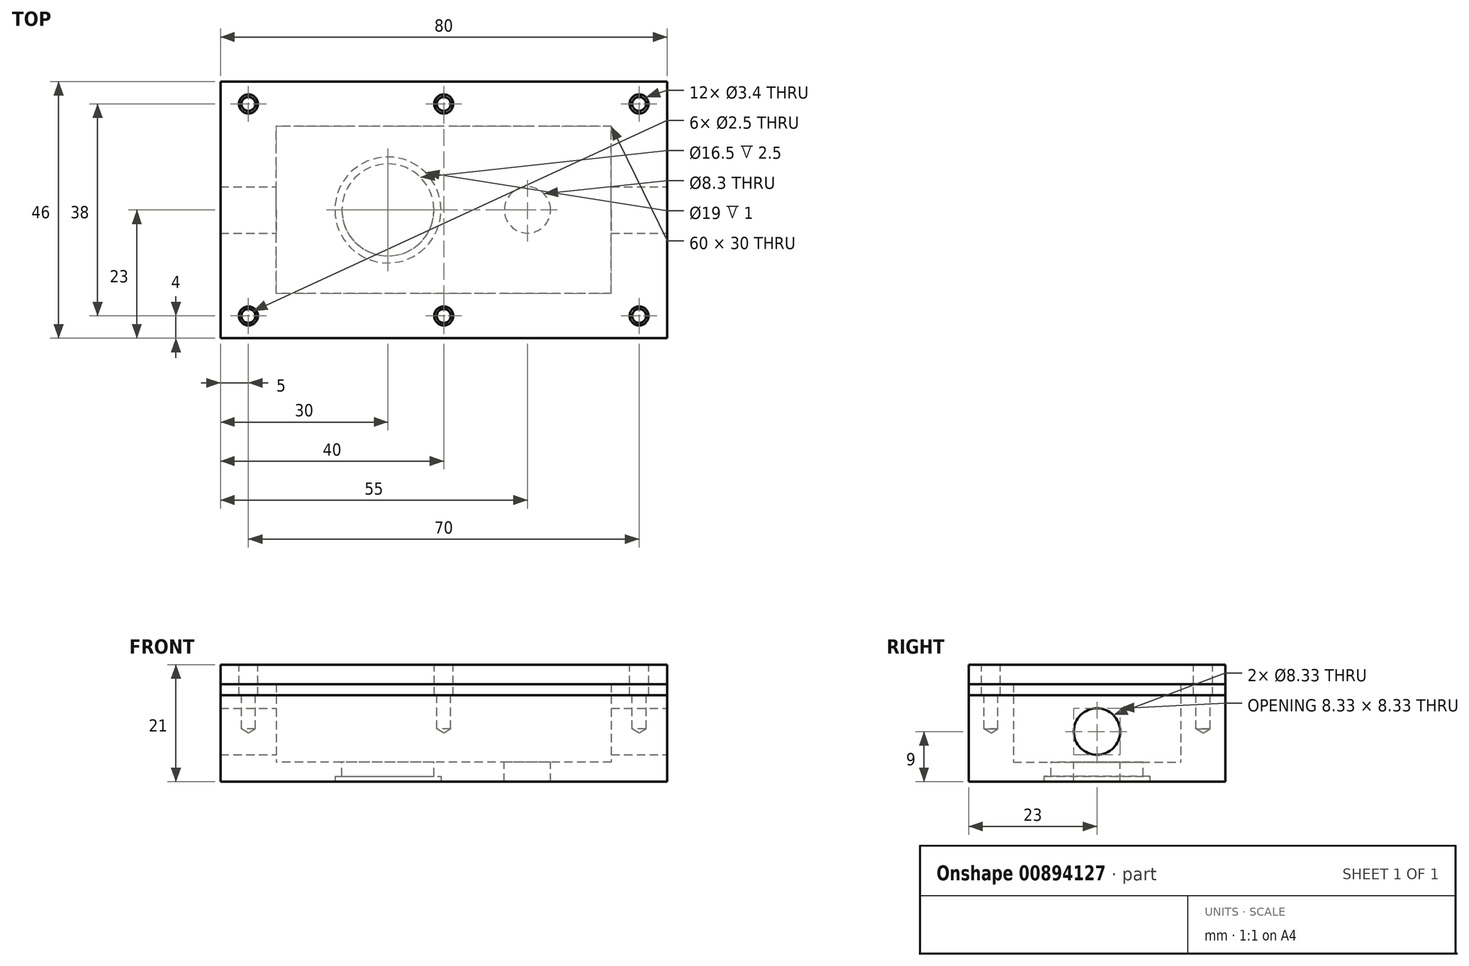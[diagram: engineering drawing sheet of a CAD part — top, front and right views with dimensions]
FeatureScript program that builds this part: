
annotation { "Feature Type Name" : "Feature", "Feature Type Description" : "" }
export const myFeature = defineFeature(function(context is Context, id is Id, definition is map)
    precondition{}
    {
        {
            var Q0;
            Q0=qCreatedBy(makeId("Top.planeOp"),FACE);
            var sketch = newSketch(context, id + "F0", { "sketchPlane" : qUnion([Q0])});
            skCircle(sketch, "E0", {"center": v(0, 0) * mm, "radius": 9.5 * mm});
            skCircle(sketch, "E1", {"center": v(0, 0) * mm, "radius": 8.25 * mm});
            skCircle(sketch, "E2", {"center": v(25, 0) * mm, "radius": 4.62 * mm});
            skCircle(sketch, "E3", {"center": v(25, 0) * mm, "radius": 4.15 * mm});
            skLineSegment(sketch, "E4.bottom", {"start": v(40, -15) * mm, "end": v(-20, -15) * mm});
            skLineSegment(sketch, "E4.top", {"start": v(40, 15) * mm, "end": v(-20, 15) * mm});
            skLineSegment(sketch, "E4.left", {"start": v(40, -15) * mm, "end": v(40, 15) * mm});
            skLineSegment(sketch, "E4.right", {"start": v(-20, -15) * mm, "end": v(-20, 15) * mm});
            skLineSegment(sketch, "E5.bottom", {"start": v(50, -23) * mm, "end": v(-30, -23) * mm});
            skLineSegment(sketch, "E5.top", {"start": v(50, 23) * mm, "end": v(-30, 23) * mm});
            skLineSegment(sketch, "E5.left", {"start": v(50, -23) * mm, "end": v(50, 23) * mm});
            skLineSegment(sketch, "E5.right", {"start": v(-30, -23) * mm, "end": v(-30, 23) * mm});
            skSolve(sketch);
        }
        {
            var Q0;
            Q0=qCreatedBy(makeId("Top.planeOp"),FACE);
            var sketch = newSketch(context, id + "F1", { "sketchPlane" : qUnion([Q0])});
            skLineSegment(sketch, "E6.0", {"start": v(50, 23) * mm, "end": v(-30, 23) * mm});
            skLineSegment(sketch, "E7.0", {"start": v(-30, -23) * mm, "end": v(-30, 23) * mm});
            skLineSegment(sketch, "E8.0", {"start": v(50, -23) * mm, "end": v(-30, -23) * mm});
            skLineSegment(sketch, "E9.0", {"start": v(50, -23) * mm, "end": v(50, 23) * mm});
            skLineSegment(sketch, "E10", {"start": v(10, 23) * mm, "end": v(10, -23) * mm, "construction": true});
            skLineSegment(sketch, "E11", {"start": v(-30, 0) * mm, "end": v(50, 0) * mm, "construction": true});
            skLineSegment(sketch, "E12", {"start": v(-25, 23) * mm, "end": v(-25, -23) * mm, "construction": true});
            skLineSegment(sketch, "E13", {"start": v(45, -23) * mm, "end": v(45, 23) * mm, "construction": true});
            skCircle(sketch, "E14", {"center": v(10, 19) * mm, "radius": 1.25 * mm});
            skCircle(sketch, "E15", {"center": v(45, 19) * mm, "radius": 1.25 * mm});
            skCircle(sketch, "E16", {"center": v(-25, 19) * mm, "radius": 1.25 * mm});
            skCircle(sketch, "E17.MirrorC", {"center": v(-25, -19) * mm, "radius": 1.25 * mm});
            skCircle(sketch, "E18.MirrorC", {"center": v(10, -19) * mm, "radius": 1.25 * mm});
            skCircle(sketch, "E19.MirrorC", {"center": v(45, -19) * mm, "radius": 1.25 * mm});
            skSolve(sketch);
        }
        {
            var Q0;
            Q0=qCreatedBy(makeId("Top.planeOp"),FACE);
            cPlane(context, id + "F2", {"entities" : qUnion([Q0]), "cplaneType" : CPlaneType.OFFSET, "offset" : 12 * mm, "width" : 150 * mm, "height" : 150 * mm});
        }
        {
            var Q0;
            Q0=qCreatedBy(makeId("Top.planeOp"),FACE);
            var sketch = newSketch(context, id + "F3", { "sketchPlane" : qUnion([Q0])});
            skLineSegment(sketch, "E20.0", {"start": v(50, -23) * mm, "end": v(-30, -23) * mm});
            skLineSegment(sketch, "E21.0", {"start": v(50, -23) * mm, "end": v(50, 23) * mm});
            skLineSegment(sketch, "E22.0", {"start": v(50, 23) * mm, "end": v(-30, 23) * mm});
            skLineSegment(sketch, "E23.0", {"start": v(-30, -23) * mm, "end": v(-30, 23) * mm});
            skSolve(sketch);
        }
        {
            var Q0;
            Q0 = qSketchRegion(id + "F3", true);
            extrude(context, id + "F4", {"entities" : qUnion([Q0]), "oppositeDirection" : true, "depth" : 3.5 * mm, "offsetDistance" : 25 * mm});
        }
        {
            var Q0;
            Q0=qCreatedBy(makeId("Top.planeOp"),FACE);
            var sketch = newSketch(context, id + "F5", { "sketchPlane" : qUnion([Q0])});
            skLineSegment(sketch, "E24.0", {"start": v(50, 23) * mm, "end": v(-30, 23) * mm});
            skLineSegment(sketch, "E25.0", {"start": v(-30, -23) * mm, "end": v(-30, 23) * mm});
            skLineSegment(sketch, "E26.0", {"start": v(-20, -15) * mm, "end": v(-20, 15) * mm});
            skLineSegment(sketch, "E27.0", {"start": v(40, 15) * mm, "end": v(-20, 15) * mm});
            skLineSegment(sketch, "E28.0", {"start": v(40, -15) * mm, "end": v(40, 15) * mm});
            skLineSegment(sketch, "E29.0", {"start": v(40, -15) * mm, "end": v(-20, -15) * mm});
            skLineSegment(sketch, "E30.0", {"start": v(50, -23) * mm, "end": v(-30, -23) * mm});
            skLineSegment(sketch, "E31.0", {"start": v(50, -23) * mm, "end": v(50, 23) * mm});
            skSolve(sketch);
        }
        {
            var Q0;
            Q0 = qSketchRegion(id + "F5", true);
            var Q1;
            Q1=qCreatedBy(id+"F2.planeOp",FACE);
            extrude(context, id + "F6", {"entities" : qUnion([Q0]), "operationType" : NewBodyOperationType.ADD, "endBound" : BoundingType.UP_TO_SURFACE, "depth" : 25 * mm, "endBoundEntityFace" : qUnion([Q1]), "offsetDistance" : 25 * mm});
        }
        {
            var Q0;
            Q0=qCreatedBy(makeId("Top.planeOp"),FACE);
            var sketch = newSketch(context, id + "F7", { "sketchPlane" : qUnion([Q0])});
            skCircle(sketch, "E32.0", {"center": v(25, 0) * mm, "radius": 4.15 * mm});
            skCircle(sketch, "E33.0", {"center": v(0, 0) * mm, "radius": 8.25 * mm});
            skSolve(sketch);
        }
        {
            var Q0;
            Q0 = qSketchRegion(id + "F7", true);
            extrude(context, id + "F8", {"entities" : qUnion([Q0]), "operationType" : NewBodyOperationType.REMOVE, "oppositeDirection" : true, "depth" : 25 * mm, "offsetDistance" : 25 * mm});
        }
        {
            var Q0;
            Q0=makeQuery(id+"F4.opExtrude","CAP_FACE",FACE,{"disambiguationData":[OSD([sQuery(id+"F3.wireOp",EDGE,"E20.0"),sQuery(id+"F3.wireOp",EDGE,"E21.0"),sQuery(id+"F3.wireOp",EDGE,"E22.0"),sQuery(id+"F3.wireOp",EDGE,"E23.0")])],"isStart":false});
            var sketch = newSketch(context, id + "F9", { "sketchPlane" : qUnion([Q0])});
            skCircle(sketch, "E34.0", {"center": v(0, 0) * mm, "radius": 9.5 * mm});
            skSolve(sketch);
        }
        {
            var Q0;
            Q0 = qSketchRegion(id + "F9", true);
            extrude(context, id + "F10", {"entities" : qUnion([Q0]), "operationType" : NewBodyOperationType.REMOVE, "oppositeDirection" : true, "depth" : 1 * mm, "offsetDistance" : 25 * mm});
        }
        {
            var Q0;
            Q0=makeQuery(id+"F6.boolean.opBoolean","MERGE",FACE,{"derivedFrom":[makeQuery(id+"F4.opExtrude","SWEPT_FACE",FACE,{"disambiguationData":[OSD([sQuery(id+"F3.wireOp",EDGE,"E21.0")])]}),makeQuery(id+"F6.opExtrude","SWEPT_FACE",FACE,{"disambiguationData":[OSD([sQuery(id+"F5.wireOp",EDGE,"E31.0")])]})]});
            cPlane(context, id + "F11", {"entities" : qUnion([Q0]), "cplaneType" : CPlaneType.OFFSET, "offset" : 0 * mm, "width" : 150 * mm, "height" : 150 * mm});
        }
        {
            var Q0;
            Q0=qCreatedBy(id+"F11.planeOp",FACE);
            var sketch = newSketch(context, id + "F12", { "sketchPlane" : qUnion([Q0])});
            skCircle(sketch, "E35", {"center": v(0, 5.5) * mm, "radius": 4.17 * mm});
            skSolve(sketch);
        }
        {
            var Q0;
            Q0=sQuery(id+"F12.wireOp",VERTEX,"E35.center");
            var Q1;
            Q1=makeQuery(id+"F4.opExtrude","SWEPT_BODY",BODY,{"disambiguationData":[OSD([sQuery(id+"F3.wireOp",EDGE,"E20.0"),sQuery(id+"F3.wireOp",EDGE,"E21.0"),sQuery(id+"F3.wireOp",EDGE,"E22.0"),sQuery(id+"F3.wireOp",EDGE,"E23.0")])]});
            hole(context, id + "F13", {"style" : HoleStyle.SIMPLE, "endStyle" : HoleEndStyle.THROUGH, "standardTappedOrClearance" : lookupTablePath({ "fit" : "Standard", "standard" : "ISO", "size" : "M3", "type" : "Clearance" }), "standardBlindInLast" : lookupTablePath({ "fit" : "Standard", "standard" : "ISO", "size" : "M3", "type" : "Clearance" }), "holeDiameter" : 8.33 * mm, "majorDiameter" : 5 * mm, "tappedDepth" : 4.5 * mm, "tapClearance" : 3, "locations" : qUnion([Q0]), "scope" : qUnion([Q1])});
        }
        {
            var Q0;
            Q0=makeQuery(id+"F6.opExtrude","CAP_FACE",FACE,{"disambiguationData":[OSD([sQuery(id+"F5.wireOp",EDGE,"E24.0"),sQuery(id+"F5.wireOp",EDGE,"E25.0"),sQuery(id+"F5.wireOp",EDGE,"E26.0"),sQuery(id+"F5.wireOp",EDGE,"E27.0"),sQuery(id+"F5.wireOp",EDGE,"E28.0"),sQuery(id+"F5.wireOp",EDGE,"E29.0"),sQuery(id+"F5.wireOp",EDGE,"E30.0"),sQuery(id+"F5.wireOp",EDGE,"E31.0")])],"isStart":false});
            var sketch = newSketch(context, id + "F14", { "sketchPlane" : qUnion([Q0])});
            skPoint(sketch, "E36.0", {"position": v(-25, 19) * mm});
            skPoint(sketch, "E37.0", {"position": v(10, 19) * mm});
            skPoint(sketch, "E38.0", {"position": v(45, 19) * mm});
            skPoint(sketch, "E39.0", {"position": v(45, -19) * mm});
            skPoint(sketch, "E40.0", {"position": v(10, -19) * mm});
            skPoint(sketch, "E41.0", {"position": v(-25, -19) * mm});
            skSolve(sketch);
        }
        {
            var Q0;
            Q0=sQuery(id+"F14.wireOp",VERTEX,"E36.0");
            var Q1;
            Q1=sQuery(id+"F14.wireOp",VERTEX,"E41.0");
            var Q2;
            Q2=sQuery(id+"F14.wireOp",VERTEX,"E40.0");
            var Q3;
            Q3=sQuery(id+"F14.wireOp",VERTEX,"E39.0");
            var Q4;
            Q4=sQuery(id+"F14.wireOp",VERTEX,"E38.0");
            var Q5;
            Q5=sQuery(id+"F14.wireOp",VERTEX,"E37.0");
            var Q6;
            Q6=makeQuery(id+"F4.opExtrude","SWEPT_BODY",BODY,{"disambiguationData":[OSD([sQuery(id+"F3.wireOp",EDGE,"E20.0"),sQuery(id+"F3.wireOp",EDGE,"E21.0"),sQuery(id+"F3.wireOp",EDGE,"E22.0"),sQuery(id+"F3.wireOp",EDGE,"E23.0")])]});
            hole(context, id + "F15", {"style" : HoleStyle.SIMPLE, "endStyle" : HoleEndStyle.BLIND, "standardTappedOrClearance" : lookupTablePath({ "standard" : "ISO", "engagement" : "75%", "pitch" : "0.5 mm", "size" : "M3", "type" : "Tapped" }), "standardBlindInLast" : lookupTablePath({ "standard" : "ISO", "engagement" : "75%", "pitch" : "0.5 mm", "size" : "M3", "type" : "Tapped" }), "holeDiameter" : 2.5 * mm, "majorDiameter" : 3 * mm, "showTappedDepth" : true, "holeDepth" : 6 * mm, "tappedDepth" : 4.5 * mm, "tapClearance" : 3, "locations" : qUnion([Q0, Q1, Q2, Q3, Q4, Q5]), "scope" : qUnion([Q6])});
        }
        {
            var Q0;
            Q0=qCreatedBy(id+"F2.planeOp",FACE);
            var sketch = newSketch(context, id + "F16", { "sketchPlane" : qUnion([Q0])});
            skLineSegment(sketch, "E42.0", {"start": v(50, 23) * mm, "end": v(-30, 23) * mm});
            skLineSegment(sketch, "E43.0", {"start": v(-30, -23) * mm, "end": v(-30, 23) * mm});
            skLineSegment(sketch, "E44.0", {"start": v(50, -23) * mm, "end": v(-30, -23) * mm});
            skLineSegment(sketch, "E45.0", {"start": v(50, -23) * mm, "end": v(50, 23) * mm});
            skLineSegment(sketch, "E46.0", {"start": v(40, -15) * mm, "end": v(40, 15) * mm});
            skLineSegment(sketch, "E47.0", {"start": v(40, 15) * mm, "end": v(-20, 15) * mm});
            skLineSegment(sketch, "E48.0", {"start": v(-20, -15) * mm, "end": v(-20, 15) * mm});
            skLineSegment(sketch, "E49.0", {"start": v(40, -15) * mm, "end": v(-20, -15) * mm});
            skSolve(sketch);
        }
        {
            var Q0;
            Q0 = qSketchRegion(id + "F16", true);
            extrude(context, id + "F17", {"entities" : qUnion([Q0]), "depth" : 2 * mm, "offsetDistance" : 25 * mm});
        }
        {
            var Q0;
            Q0=makeQuery(id+"F17.opExtrude","CAP_FACE",FACE,{"disambiguationData":[OSD([sQuery(id+"F16.wireOp",EDGE,"E42.0"),sQuery(id+"F16.wireOp",EDGE,"E43.0"),sQuery(id+"F16.wireOp",EDGE,"E44.0"),sQuery(id+"F16.wireOp",EDGE,"E45.0"),sQuery(id+"F16.wireOp",EDGE,"E46.0"),sQuery(id+"F16.wireOp",EDGE,"E47.0"),sQuery(id+"F16.wireOp",EDGE,"E48.0"),sQuery(id+"F16.wireOp",EDGE,"E49.0")])],"isStart":false});
            var sketch = newSketch(context, id + "F18", { "sketchPlane" : qUnion([Q0])});
            skPoint(sketch, "E50.0", {"position": v(-25, 19) * mm});
            skPoint(sketch, "E51.0", {"position": v(10, 19) * mm});
            skPoint(sketch, "E52.0", {"position": v(45, 19) * mm});
            skPoint(sketch, "E53.0", {"position": v(45, -19) * mm});
            skPoint(sketch, "E54.0", {"position": v(10, -19) * mm});
            skPoint(sketch, "E55.0", {"position": v(-25, -19) * mm});
            skSolve(sketch);
        }
        {
            var Q0;
            Q0=sQuery(id+"F18.wireOp",VERTEX,"E55.0");
            var Q1;
            Q1=sQuery(id+"F18.wireOp",VERTEX,"E54.0");
            var Q2;
            Q2=sQuery(id+"F18.wireOp",VERTEX,"E53.0");
            var Q3;
            Q3=sQuery(id+"F18.wireOp",VERTEX,"E52.0");
            var Q4;
            Q4=sQuery(id+"F18.wireOp",VERTEX,"E51.0");
            var Q5;
            Q5=sQuery(id+"F18.wireOp",VERTEX,"E50.0");
            var Q6;
            Q6=makeQuery(id+"F17.opExtrude","SWEPT_BODY",BODY,{"disambiguationData":[OSD([sQuery(id+"F16.wireOp",EDGE,"E42.0"),sQuery(id+"F16.wireOp",EDGE,"E43.0"),sQuery(id+"F16.wireOp",EDGE,"E44.0"),sQuery(id+"F16.wireOp",EDGE,"E45.0"),sQuery(id+"F16.wireOp",EDGE,"E46.0"),sQuery(id+"F16.wireOp",EDGE,"E47.0"),sQuery(id+"F16.wireOp",EDGE,"E48.0"),sQuery(id+"F16.wireOp",EDGE,"E49.0")])]});
            hole(context, id + "F19", {"style" : HoleStyle.SIMPLE, "endStyle" : HoleEndStyle.THROUGH, "standardTappedOrClearance" : lookupTablePath({ "fit" : "Normal", "standard" : "ISO", "size" : "M3", "type" : "Clearance" }), "standardBlindInLast" : lookupTablePath({ "fit" : "Normal", "standard" : "ISO", "size" : "M3", "type" : "Clearance" }), "holeDiameter" : 3.4 * mm, "majorDiameter" : 3 * mm, "tappedDepth" : 4.5 * mm, "tapClearance" : 3, "locations" : qUnion([Q0, Q1, Q2, Q3, Q4, Q5]), "scope" : qUnion([Q6])});
        }
        {
            var Q0;
            Q0=makeQuery(id+"F17.opExtrude","CAP_FACE",FACE,{"disambiguationData":[OSD([sQuery(id+"F16.wireOp",EDGE,"E42.0"),sQuery(id+"F16.wireOp",EDGE,"E43.0"),sQuery(id+"F16.wireOp",EDGE,"E44.0"),sQuery(id+"F16.wireOp",EDGE,"E45.0"),sQuery(id+"F16.wireOp",EDGE,"E46.0"),sQuery(id+"F16.wireOp",EDGE,"E47.0"),sQuery(id+"F16.wireOp",EDGE,"E48.0"),sQuery(id+"F16.wireOp",EDGE,"E49.0")])],"isStart":false});
            var sketch = newSketch(context, id + "F20", { "sketchPlane" : qUnion([Q0])});
            skLineSegment(sketch, "E56.0", {"start": v(50, -23) * mm, "end": v(-30, -23) * mm});
            skLineSegment(sketch, "E57.0", {"start": v(50, -23) * mm, "end": v(50, 23) * mm});
            skLineSegment(sketch, "E58.0", {"start": v(50, 23) * mm, "end": v(-30, 23) * mm});
            skLineSegment(sketch, "E59.0", {"start": v(-30, -23) * mm, "end": v(-30, 23) * mm});
            skSolve(sketch);
        }
        {
            var Q0;
            Q0 = qSketchRegion(id + "F20", true);
            extrude(context, id + "F21", {"entities" : qUnion([Q0]), "depth" : 3.5 * mm, "offsetDistance" : 25 * mm});
        }
        {
            var Q0;
            Q0=makeQuery(id+"F21.opExtrude","CAP_FACE",FACE,{"disambiguationData":[OSD([sQuery(id+"F20.wireOp",EDGE,"E56.0"),sQuery(id+"F20.wireOp",EDGE,"E57.0"),sQuery(id+"F20.wireOp",EDGE,"E58.0"),sQuery(id+"F20.wireOp",EDGE,"E59.0")])],"isStart":false});
            var sketch = newSketch(context, id + "F22", { "sketchPlane" : qUnion([Q0])});
            skPoint(sketch, "E60.0", {"position": v(45, -19) * mm});
            skPoint(sketch, "E61.0", {"position": v(45, 19) * mm});
            skPoint(sketch, "E62.0", {"position": v(10, 19) * mm});
            skPoint(sketch, "E63.0", {"position": v(-25, 19) * mm});
            skPoint(sketch, "E64.0", {"position": v(-25, -19) * mm});
            skPoint(sketch, "E65.0", {"position": v(10, -19) * mm});
            skSolve(sketch);
        }
        {
            var Q0;
            Q0=sQuery(id+"F22.wireOp",VERTEX,"E60.0");
            var Q1;
            Q1=sQuery(id+"F22.wireOp",VERTEX,"E61.0");
            var Q2;
            Q2=sQuery(id+"F22.wireOp",VERTEX,"E62.0");
            var Q3;
            Q3=sQuery(id+"F22.wireOp",VERTEX,"E63.0");
            var Q4;
            Q4=sQuery(id+"F22.wireOp",VERTEX,"E64.0");
            var Q5;
            Q5=sQuery(id+"F22.wireOp",VERTEX,"E65.0");
            var Q6;
            Q6=makeQuery(id+"F21.opExtrude","SWEPT_BODY",BODY,{"disambiguationData":[OSD([sQuery(id+"F20.wireOp",EDGE,"E56.0"),sQuery(id+"F20.wireOp",EDGE,"E57.0"),sQuery(id+"F20.wireOp",EDGE,"E58.0"),sQuery(id+"F20.wireOp",EDGE,"E59.0")])]});
            hole(context, id + "F23", {"style" : HoleStyle.SIMPLE, "endStyle" : HoleEndStyle.BLIND, "standardTappedOrClearance" : lookupTablePath({ "fit" : "Normal", "standard" : "ISO", "size" : "M3", "type" : "Clearance" }), "standardBlindInLast" : lookupTablePath({ "fit" : "Normal", "standard" : "ISO", "size" : "M3", "type" : "Clearance" }), "holeDiameter" : 3.4 * mm, "majorDiameter" : 5 * mm, "holeDepth" : 6 * mm, "tappedDepth" : 4.5 * mm, "tapClearance" : 3, "locations" : qUnion([Q0, Q1, Q2, Q3, Q4, Q5]), "scope" : qUnion([Q6])});
        }
    });
